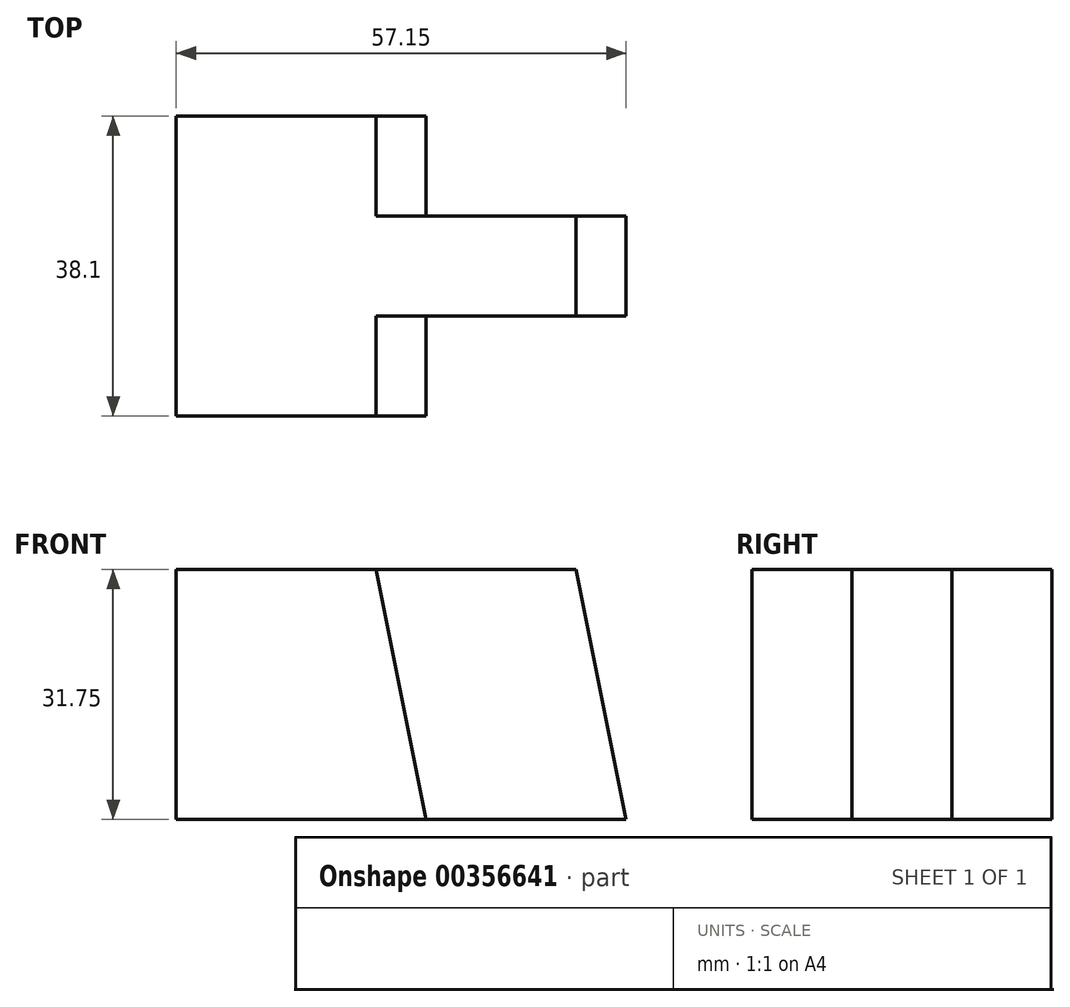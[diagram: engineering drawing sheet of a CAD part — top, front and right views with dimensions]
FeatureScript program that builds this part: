
annotation { "Feature Type Name" : "Feature", "Feature Type Description" : "" }
export const myFeature = defineFeature(function(context is Context, id is Id, definition is map)
    precondition{}
    {
        {
            var Q0;
            Q0=qCreatedBy(makeId("Front.planeOp"),FACE);
            var sketch = newSketch(context, id + "F0", { "sketchPlane" : qUnion([Q0])});
            skLineSegment(sketch, "E0", {"start": v(-39.65, 0) * mm, "end": v(17.5, 0) * mm});
            skLineSegment(sketch, "E1", {"start": v(17.5, 0) * mm, "end": v(17.5, 31.75) * mm});
            skLineSegment(sketch, "E2", {"start": v(17.5, 31.75) * mm, "end": v(-39.65, 31.75) * mm});
            skLineSegment(sketch, "E3", {"start": v(-39.65, 31.75) * mm, "end": v(-39.65, 0) * mm});
            skSolve(sketch);
        }
        {
            var Q0;
            Q0 = qSketchRegion(id + "F0", true);
            extrude(context, id + "F1", {"entities" : qUnion([Q0]), "depth" : 38.1 * mm});
        }
        {
            var Q0;
            Q0=makeQuery(id+"F1.opExtrude","CAP_FACE",FACE,{"disambiguationData":[OSD([sQuery(id+"F0.wireOp",EDGE,"E0"),sQuery(id+"F0.wireOp",EDGE,"E1"),sQuery(id+"F0.wireOp",EDGE,"E2"),sQuery(id+"F0.wireOp",EDGE,"E3")])],"isStart":false});
            var sketch = newSketch(context, id + "F2", { "sketchPlane" : qUnion([Q0])});
            skLineSegment(sketch, "E4", {"start": v(-14.25, 31.75) * mm, "end": v(-7.9, 0) * mm});
            skLineSegment(sketch, "E5", {"start": v(-7.9, 0) * mm, "end": v(17.5, 0) * mm});
            skLineSegment(sketch, "E6", {"start": v(17.5, 0) * mm, "end": v(17.5, 31.75) * mm});
            skLineSegment(sketch, "E7", {"start": v(17.5, 31.75) * mm, "end": v(-14.25, 31.75) * mm});
            skSolve(sketch);
        }
        {
            var Q0;
            Q0=makeQuery(id+"F2.imprint","IMPRINT",FACE,{"disambiguationData":[TD([[makeQuery(id+"F2.imprint","IMPRINT",EDGE,{"derivedFrom":sQuery(id+"F2.wireOp",EDGE,"E4")}),1.0]])]});
            extrude(context, id + "F3", {"entities" : qUnion([Q0]), "operationType" : NewBodyOperationType.REMOVE, "oppositeDirection" : true, "depth" : 12.7 * mm});
        }
        {
            var Q0;
            Q0=makeQuery(id+"F1.opExtrude","CAP_FACE",FACE,{"disambiguationData":[OSD([sQuery(id+"F0.wireOp",EDGE,"E0"),sQuery(id+"F0.wireOp",EDGE,"E1"),sQuery(id+"F0.wireOp",EDGE,"E2"),sQuery(id+"F0.wireOp",EDGE,"E3")])],"isStart":true});
            var sketch = newSketch(context, id + "F4", { "sketchPlane" : qUnion([Q0])});
            skLineSegment(sketch, "E8", {"start": v(-17.5, 31.75) * mm, "end": v(-17.5, 0) * mm});
            skLineSegment(sketch, "E9", {"start": v(-17.5, 0) * mm, "end": v(7.9, 0) * mm});
            skLineSegment(sketch, "E10", {"start": v(7.9, 0) * mm, "end": v(14.25, 31.75) * mm});
            skLineSegment(sketch, "E11", {"start": v(14.25, 31.75) * mm, "end": v(-17.5, 31.75) * mm});
            skSolve(sketch);
        }
        {
            var Q0;
            Q0 = qSketchRegion(id + "F4", true);
            extrude(context, id + "F5", {"entities" : qUnion([Q0]), "operationType" : NewBodyOperationType.REMOVE, "oppositeDirection" : true, "depth" : 12.7 * mm});
        }
        {
            var Q0;
            Q0=makeQuery(id+"F3.boolean.opBoolean","COPY",FACE,{"derivedFrom":makeQuery(id+"F3.opExtrude","CAP_FACE",FACE,{"disambiguationData":[OSD([sQuery(id+"F2.wireOp",EDGE,"E4"),sQuery(id+"F2.wireOp",EDGE,"E5"),sQuery(id+"F2.wireOp",EDGE,"E6"),sQuery(id+"F2.wireOp",EDGE,"E7")])],"isStart":false})});
            var sketch = newSketch(context, id + "F6", { "sketchPlane" : qUnion([Q0])});
            skLineSegment(sketch, "E12", {"start": v(17.5, 0) * mm, "end": v(11.15, 31.75) * mm});
            skLineSegment(sketch, "E13", {"start": v(11.15, 31.75) * mm, "end": v(17.5, 31.75) * mm});
            skLineSegment(sketch, "E14", {"start": v(17.5, 31.75) * mm, "end": v(17.5, 0) * mm});
            skSolve(sketch);
        }
        {
            var Q0;
            Q0 = qSketchRegion(id + "F6", true);
            extrude(context, id + "F7", {"entities" : qUnion([Q0]), "operationType" : NewBodyOperationType.REMOVE, "oppositeDirection" : true, "depth" : 25.4 * mm});
        }
    });
